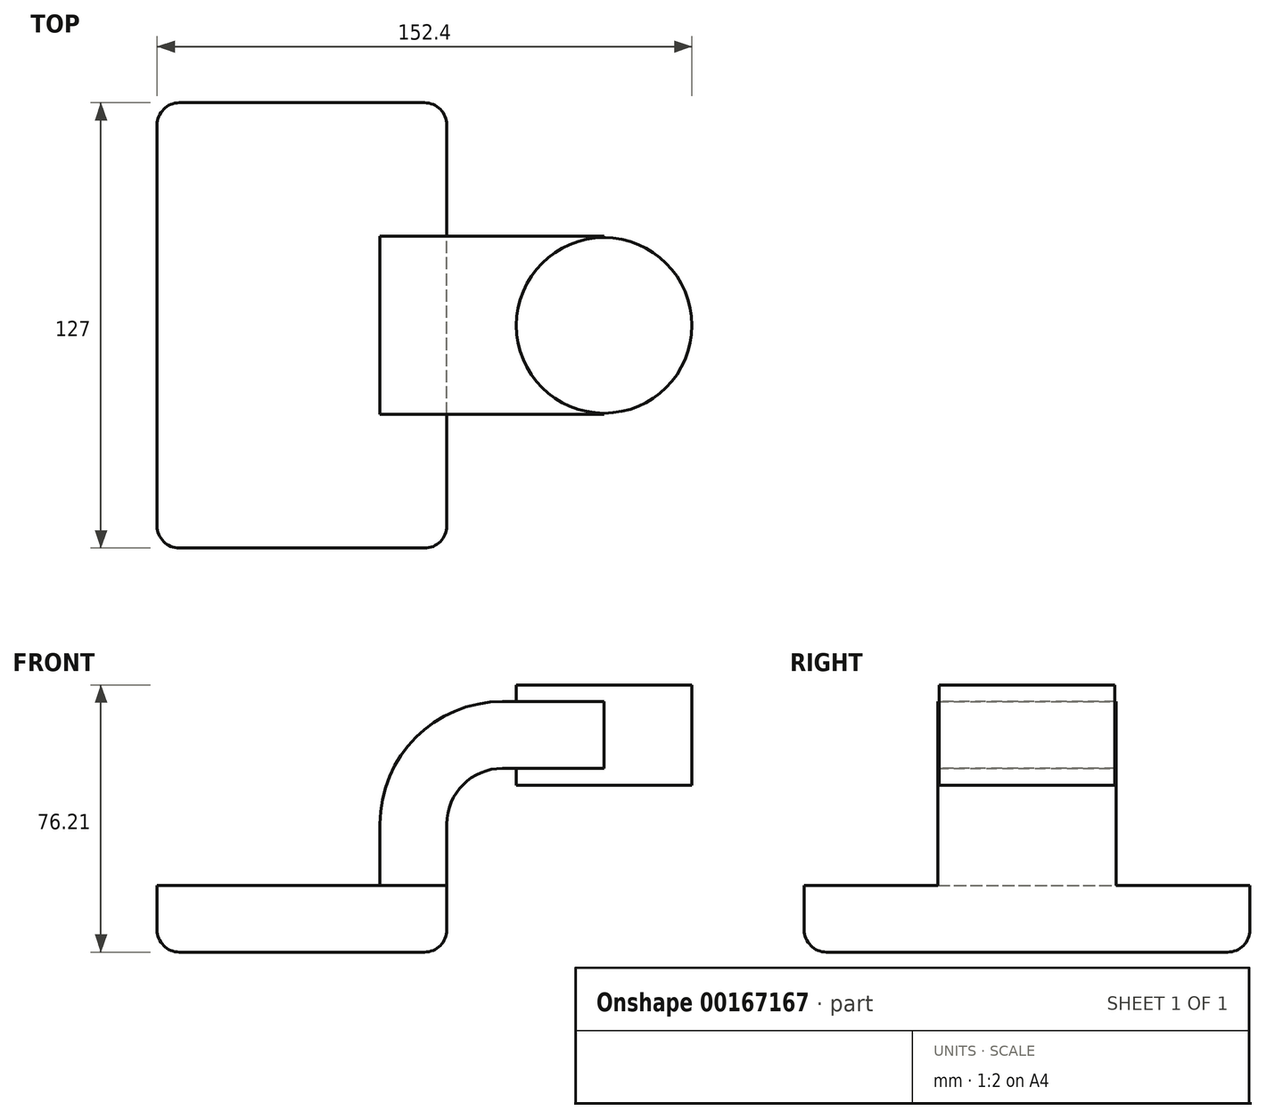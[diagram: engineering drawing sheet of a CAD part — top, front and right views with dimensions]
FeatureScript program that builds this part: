
annotation { "Feature Type Name" : "Feature", "Feature Type Description" : "" }
export const myFeature = defineFeature(function(context is Context, id is Id, definition is map)
    precondition{}
    {
        {
            var Q0;
            Q0=qCreatedBy(makeId("Front.planeOp"),FACE);
            var sketch = newSketch(context, id + "F0", { "sketchPlane" : qUnion([Q0])});
            skLineSegment(sketch, "E0.bottom", {"start": v(-41.28, 9.52) * mm, "end": v(41.28, 9.53) * mm});
            skLineSegment(sketch, "E0.top", {"start": v(-41.28, -9.53) * mm, "end": v(41.28, -9.53) * mm});
            skLineSegment(sketch, "E0.left", {"start": v(-41.28, 9.52) * mm, "end": v(-41.28, -9.53) * mm});
            skLineSegment(sketch, "E0.right", {"start": v(41.28, 9.53) * mm, "end": v(41.28, -9.52) * mm});
            skPoint(sketch, "E0.middle", {"position": v(0, 0) * mm});
            skLineSegment(sketch, "E1.bottom", {"start": v(60.32, 66.68) * mm, "end": v(111.12, 66.68) * mm});
            skLineSegment(sketch, "E1.top", {"start": v(60.32, 38.1) * mm, "end": v(111.12, 38.1) * mm});
            skLineSegment(sketch, "E1.left", {"start": v(60.32, 66.68) * mm, "end": v(60.32, 38.1) * mm});
            skLineSegment(sketch, "E1.right", {"start": v(111.12, 66.68) * mm, "end": v(111.12, 38.1) * mm});
            skPoint(sketch, "E1.middle", {"position": v(85.72, 52.39) * mm});
            skLineSegment(sketch, "E2", {"start": v(41.27, 9.53) * mm, "end": v(41.27, 27) * mm});
            skArc(sketch, "E3", {"start": v(41.27, 27) * mm, "mid": v(45.92, 38.23) * mm, "end": v(57.15, 42.88) * mm});
            skLineSegment(sketch, "E4", {"start": v(57.15, 42.88) * mm, "end": v(86.1, 42.88) * mm});
            skLineSegment(sketch, "E5.0", {"start": v(57.15, 61.93) * mm, "end": v(86.1, 61.93) * mm});
            skArc(sketch, "E5.1", {"start": v(22.22, 27) * mm, "mid": v(32.45, 51.7) * mm, "end": v(57.15, 61.93) * mm});
            skLineSegment(sketch, "E5.2", {"start": v(22.22, 9.53) * mm, "end": v(22.22, 27) * mm});
            skLineSegment(sketch, "E6", {"start": v(86.1, 61.93) * mm, "end": v(86.1, 42.88) * mm});
            skFitSpline(sketch, "E7", {"points": [v(-41.28, 9.52) * mm, v(57.15, 61.93) * mm], "startDerivative": vector(88.92, 102.75) * mm, "endDerivative": vector(126.18, -5.87) * mm});
            skLineSegment(sketch, "E8", {"start": v(86.1, 66.68) * mm, "end": v(86.1, 38.1) * mm});
            skSolve(sketch);
        }
        {
            var Q0;
            Q0=makeQuery(id+"F0.imprint","IMPRINT",FACE,{"disambiguationData":[TD([[makeQuery(id+"F0.imprint","IMPRINT",EDGE,{"derivedFrom":sQuery(id+"F0.wireOp",EDGE,"E0.top")}),1.0]])]});
            extrude(context, id + "F1", {"entities" : qUnion([Q0]), "endBound" : BoundingType.SYMMETRIC, "depth" : 127 * mm});
        }
        {
            var Q0;
            {var subQ1=sQuery(id+"F0.wireOp",EDGE,"E2");Q0=makeQuery(id+"F0.imprint","IMPRINT",FACE,{"disambiguationData":[TD([[makeQuery(id+"F0.imprint","IMPRINT",EDGE,{"derivedFrom":subQ1}),1.0]])]});}
            var Q1;
            {var subQ5=sQuery(id+"F0.wireOp",EDGE,"E6");Q1=makeQuery(id+"F0.imprint","IMPRINT",FACE,{"disambiguationData":[TD([[makeQuery(id+"F0.imprint","IMPRINT",EDGE,{"derivedFrom":subQ5}),-1.0]])]});}
            extrude(context, id + "F2", {"entities" : qUnion([Q0, Q1]), "operationType" : NewBodyOperationType.ADD, "endBound" : BoundingType.SYMMETRIC, "depth" : 50.8 * mm});
        }
        {
            var Q0;
            Q0=makeQuery(id+"F0.imprint","IMPRINT",FACE,{"disambiguationData":[TD([[makeQuery(id+"F0.imprint","IMPRINT",EDGE,{"derivedFrom":sQuery(id+"F0.wireOp",EDGE,"E5.1")}),1.0]])]});
            extrude(context, id + "F3", {"entities" : qUnion([Q0]), "operationType" : NewBodyOperationType.ADD, "depth" : 15.88 * mm});
        }
        {
            var Q0;
            {var subQ0=sQuery(id+"F0.wireOp",EDGE,"E5.0");var subQ1=sQuery(id+"F0.wireOp",EDGE,"E1.left");var subQ2=makeQuery(id+"F0.imprint","INTERSECT",VERTEX,{"derivedFrom":[subQ1,subQ0]});Q0=makeQuery(id+"F0.imprint","IMPRINT",FACE,{"disambiguationData":[TD([[makeQuery(id+"F0.imprint","IMPRINT",EDGE,{"disambiguationData":[TD([[subQ2,-1.0]])],"derivedFrom":subQ1}),1.0]])]});}
            extrude(context, id + "F4", {"entities" : qUnion([Q0]), "operationType" : NewBodyOperationType.ADD, "endBound" : BoundingType.SYMMETRIC, "depth" : 50.8 * mm});
        }
        {
            var Q0;
            {var subQ0=sQuery(id+"F0.wireOp",EDGE,"E1.right");Q0=makeQuery(id+"F0.imprint","IMPRINT",FACE,{"disambiguationData":[TD([[makeQuery(id+"F0.imprint","IMPRINT",EDGE,{"derivedFrom":subQ0}),-1.0]])]});}
            var Q1;
            Q1=sQuery(id+"F0.wireOp",EDGE,"E8");
            revolve(context, id + "F5", {"operationType" : NewBodyOperationType.ADD, "entities" : qUnion([Q0]), "axis" : qUnion([Q1]), "revolveType" : RevolveType.FULL});
        }
        {
            var Q0;
            Q0=makeQuery(id+"F1.opExtrude","CAP_EDGE",EDGE,{"disambiguationData":[OSD([sQuery(id+"F0.wireOp",EDGE,"E0.right")])],"isStart":false});
            var Q1;
            Q1=makeQuery(id+"F1.opExtrude","CAP_EDGE",EDGE,{"disambiguationData":[OSD([sQuery(id+"F0.wireOp",EDGE,"E0.left")])],"isStart":false});
            var Q2;
            Q2=makeQuery(id+"F1.opExtrude","SWEPT_FACE",FACE,{"disambiguationData":[OSD([sQuery(id+"F0.wireOp",EDGE,"E0.top")])]});
            var Q3;
            Q3=makeQuery(id+"F1.opExtrude","CAP_EDGE",EDGE,{"disambiguationData":[OSD([sQuery(id+"F0.wireOp",EDGE,"E0.left")])],"isStart":true});
            var Q4;
            Q4=makeQuery(id+"F1.opExtrude","CAP_EDGE",EDGE,{"disambiguationData":[OSD([sQuery(id+"F0.wireOp",EDGE,"E0.right")])],"isStart":true});
            fillet(context, id + "F6", {"entities" : qUnion([Q0, Q1, Q2, Q3, Q4]), "radius" : 6.35 * mm, "tangentPropagation" : true, "allowEdgeOverflow" : false});
        }
    });
